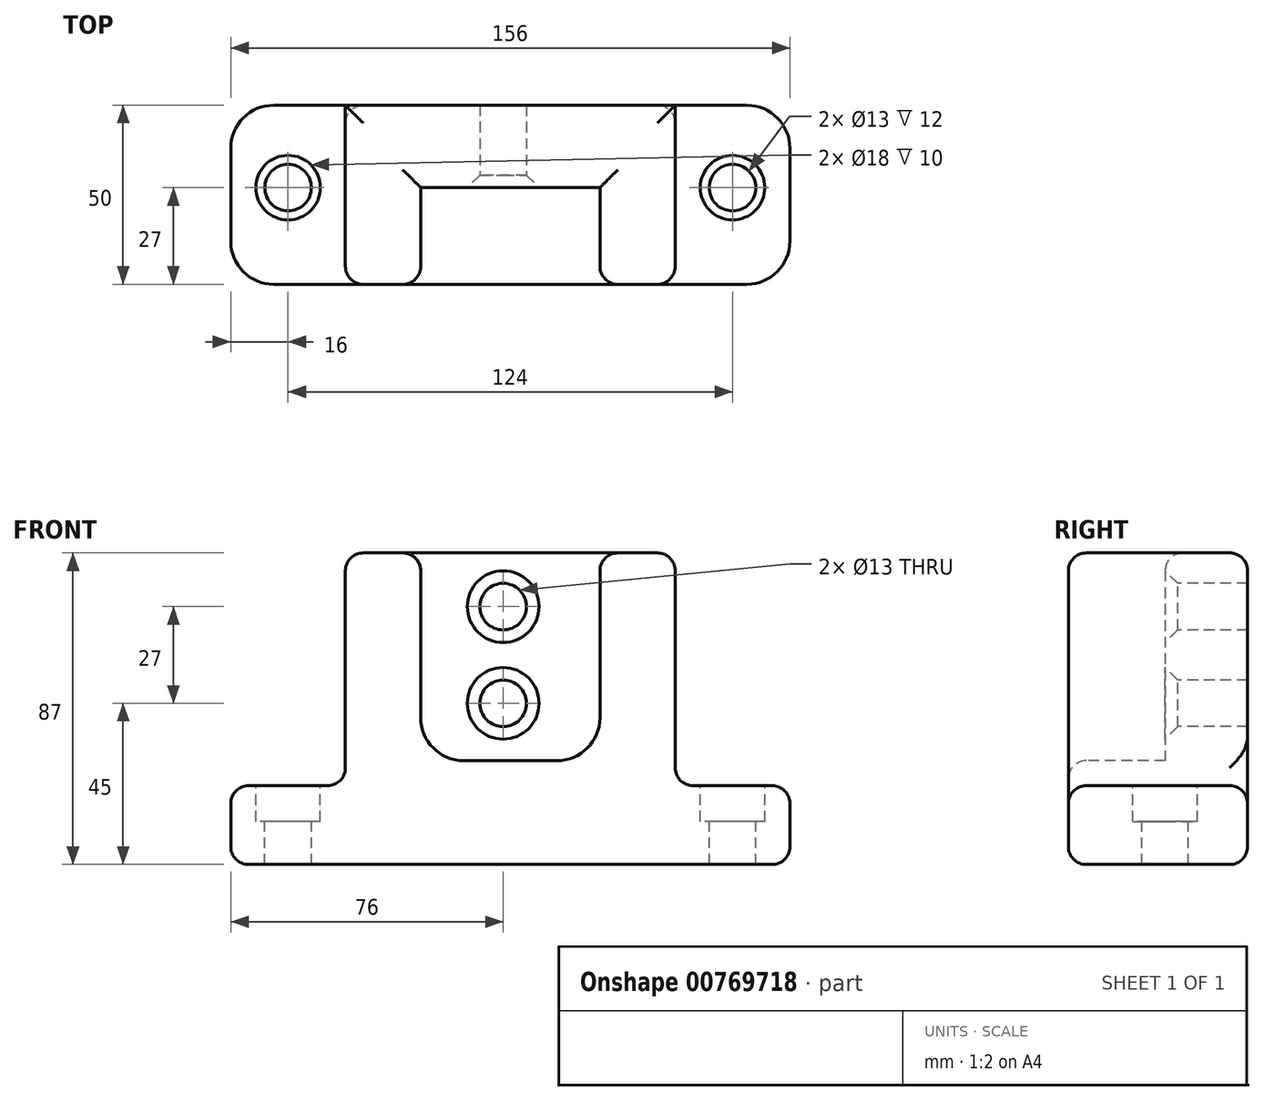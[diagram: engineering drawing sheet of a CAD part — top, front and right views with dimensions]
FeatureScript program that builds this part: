
annotation { "Feature Type Name" : "Feature", "Feature Type Description" : "" }
export const myFeature = defineFeature(function(context is Context, id is Id, definition is map)
    precondition{}
    {
        {
            var Q0;
            Q0=qCreatedBy(makeId("Top.planeOp"),FACE);
            var sketch = newSketch(context, id + "F0", { "sketchPlane" : qUnion([Q0])});
            skLineSegment(sketch, "E0.bottom", {"start": v(0, 0) * mm, "end": v(156, 0) * mm});
            skLineSegment(sketch, "E0.top", {"start": v(0, 50) * mm, "end": v(156, 50) * mm});
            skLineSegment(sketch, "E0.left", {"start": v(0, 0) * mm, "end": v(0, 50) * mm});
            skLineSegment(sketch, "E0.right", {"start": v(156, 0) * mm, "end": v(156, 50) * mm});
            skSolve(sketch);
        }
        {
            var Q0;
            Q0=makeQuery(id+"F0.imprint","IMPRINT",FACE,{"disambiguationData":[TD([[makeQuery(id+"F0.imprint","IMPRINT",EDGE,{"derivedFrom":sQuery(id+"F0.wireOp",EDGE,"E0.bottom")}),1.0]])]});
            extrude(context, id + "F1", {"entities" : qUnion([Q0]), "depth" : 87 * mm, "offsetDistance" : 25 * mm});
        }
        {
            var Q0;
            Q0=makeQuery(id+"F1.opExtrude","SWEPT_FACE",FACE,{"disambiguationData":[OSD([sQuery(id+"F0.wireOp",EDGE,"E0.bottom")])]});
            var sketch = newSketch(context, id + "F2", { "sketchPlane" : qUnion([Q0])});
            skLineSegment(sketch, "E1.bottom", {"start": v(0, 87) * mm, "end": v(32, 87) * mm});
            skLineSegment(sketch, "E1.top", {"start": v(0, 22) * mm, "end": v(32, 22) * mm});
            skLineSegment(sketch, "E1.left", {"start": v(0, 87) * mm, "end": v(0, 22) * mm});
            skLineSegment(sketch, "E1.right", {"start": v(32, 87) * mm, "end": v(32, 22) * mm});
            skLineSegment(sketch, "E2.bottom", {"start": v(156, 87) * mm, "end": v(124, 87) * mm});
            skLineSegment(sketch, "E2.top", {"start": v(156, 22) * mm, "end": v(124, 22) * mm});
            skLineSegment(sketch, "E2.left", {"start": v(156, 87) * mm, "end": v(156, 22) * mm});
            skLineSegment(sketch, "E2.right", {"start": v(124, 87) * mm, "end": v(124, 22) * mm});
            skSolve(sketch);
        }
        {
            var Q0;
            Q0 = qSketchRegion(id + "F2", true);
            extrude(context, id + "F3", {"entities" : qUnion([Q0]), "operationType" : NewBodyOperationType.REMOVE, "endBound" : BoundingType.UP_TO_NEXT, "oppositeDirection" : true, "depth" : 25 * mm, "offsetDistance" : 25 * mm});
        }
        {
            var Q0;
            Q0=makeQuery(id+"F1.opExtrude","SWEPT_FACE",FACE,{"disambiguationData":[OSD([sQuery(id+"F0.wireOp",EDGE,"E0.bottom")])]});
            var sketch = newSketch(context, id + "F4", { "sketchPlane" : qUnion([Q0])});
            skLineSegment(sketch, "E3.bottom", {"start": v(53, 87) * mm, "end": v(103, 87) * mm});
            skLineSegment(sketch, "E3.top", {"start": v(53, 29) * mm, "end": v(103, 29) * mm});
            skLineSegment(sketch, "E3.left", {"start": v(53, 87) * mm, "end": v(53, 29) * mm});
            skLineSegment(sketch, "E3.right", {"start": v(103, 87) * mm, "end": v(103, 29) * mm});
            skSolve(sketch);
        }
        {
            var Q0;
            Q0=makeQuery(id+"F4.imprint","IMPRINT",FACE,{"disambiguationData":[TD([[makeQuery(id+"F4.imprint","IMPRINT",EDGE,{"derivedFrom":sQuery(id+"F4.wireOp",EDGE,"E3.bottom")}),-1.0]])]});
            extrude(context, id + "F5", {"entities" : qUnion([Q0]), "operationType" : NewBodyOperationType.REMOVE, "oppositeDirection" : true, "depth" : 27 * mm, "offsetDistance" : 25 * mm});
        }
        {
            var Q0;
            Q0=makeQuery(id+"F3.boolean.opBoolean","COPY",FACE,{"derivedFrom":makeQuery(id+"F3.opExtrude","SWEPT_FACE",FACE,{"disambiguationData":[OSD([sQuery(id+"F2.wireOp",EDGE,"E2.top")])]})});
            var sketch = newSketch(context, id + "F6", { "sketchPlane" : qUnion([Q0])});
            skPoint(sketch, "E4", {"position": v(16, 27) * mm});
            skPoint(sketch, "E5", {"position": v(140, 27) * mm});
            skSolve(sketch);
        }
        {
            var Q0;
            Q0=sQuery(id+"F6.wireOp",VERTEX,"E4");
            var Q1;
            Q1=sQuery(id+"F6.wireOp",VERTEX,"E5");
            var Q2;
            Q2=makeQuery(id+"F1.opExtrude","SWEPT_BODY",BODY,{"disambiguationData":[OSD([sQuery(id+"F0.wireOp",EDGE,"E0.bottom"),sQuery(id+"F0.wireOp",EDGE,"E0.top"),sQuery(id+"F0.wireOp",EDGE,"E0.left"),sQuery(id+"F0.wireOp",EDGE,"E0.right")])]});
            hole(context, id + "F7", {"style" : HoleStyle.C_BORE, "endStyle" : HoleEndStyle.THROUGH, "holeDiameter" : 13 * mm, "cBoreDiameter" : 18 * mm, "cBoreDepth" : 10 * mm, "majorDiameter" : 5 * mm, "isTappedThrough" : true, "tappedDepth" : 12 * mm, "tapClearance" : 3, "locations" : qUnion([Q0, Q1]), "scope" : qUnion([Q2])});
        }
        {
            var Q0;
            Q0=makeQuery(id+"F5.boolean.opBoolean","COPY",FACE,{"derivedFrom":makeQuery(id+"F5.opExtrude","CAP_FACE",FACE,{"disambiguationData":[OSD([sQuery(id+"F4.wireOp",EDGE,"E3.bottom"),sQuery(id+"F4.wireOp",EDGE,"E3.top"),sQuery(id+"F4.wireOp",EDGE,"E3.left"),sQuery(id+"F4.wireOp",EDGE,"E3.right")])],"isStart":false})});
            var sketch = newSketch(context, id + "F8", { "sketchPlane" : qUnion([Q0])});
            skPoint(sketch, "E6", {"position": v(76, 72) * mm});
            skPoint(sketch, "E7", {"position": v(76, 45) * mm});
            skSolve(sketch);
        }
        {
            var Q0;
            Q0=sQuery(id+"F8.wireOp",VERTEX,"E6");
            var Q1;
            Q1=sQuery(id+"F8.wireOp",VERTEX,"E7");
            var Q2;
            Q2=makeQuery(id+"F1.opExtrude","SWEPT_BODY",BODY,{"disambiguationData":[OSD([sQuery(id+"F0.wireOp",EDGE,"E0.bottom"),sQuery(id+"F0.wireOp",EDGE,"E0.top"),sQuery(id+"F0.wireOp",EDGE,"E0.left"),sQuery(id+"F0.wireOp",EDGE,"E0.right")])]});
            hole(context, id + "F9", {"style" : HoleStyle.C_SINK, "endStyle" : HoleEndStyle.THROUGH, "holeDiameter" : 13 * mm, "cSinkDiameter" : 20 * mm, "cSinkAngle" : 90 * degree, "majorDiameter" : 5 * mm, "isTappedThrough" : true, "tappedDepth" : 12 * mm, "tapClearance" : 3, "locations" : qUnion([Q0, Q1]), "scope" : qUnion([Q2])});
        }
        {
            var Q0;
            Q0=makeQuery(id+"F1.opExtrude","SWEPT_EDGE",EDGE,{"disambiguationData":[OSD([sQuery(id+"F0.wireOp",EDGE,"E0.bottom"),sQuery(id+"F0.wireOp",EDGE,"E0.right")])]});
            var Q1;
            Q1=makeQuery(id+"F1.opExtrude","SWEPT_EDGE",EDGE,{"disambiguationData":[OSD([sQuery(id+"F0.wireOp",EDGE,"E0.top"),sQuery(id+"F0.wireOp",EDGE,"E0.right")])]});
            var Q2;
            Q2=makeQuery(id+"F5.boolean.opBoolean","COPY",EDGE,{"derivedFrom":makeQuery(id+"F5.opExtrude","SWEPT_EDGE",EDGE,{"disambiguationData":[OSD([sQuery(id+"F4.wireOp",EDGE,"E3.top"),sQuery(id+"F4.wireOp",EDGE,"E3.right")])]})});
            var Q3;
            Q3=makeQuery(id+"F5.boolean.opBoolean","COPY",EDGE,{"derivedFrom":makeQuery(id+"F5.opExtrude","SWEPT_EDGE",EDGE,{"disambiguationData":[OSD([sQuery(id+"F4.wireOp",EDGE,"E3.top"),sQuery(id+"F4.wireOp",EDGE,"E3.left")])]})});
            var Q4;
            Q4=makeQuery(id+"F1.opExtrude","SWEPT_EDGE",EDGE,{"disambiguationData":[OSD([sQuery(id+"F0.wireOp",EDGE,"E0.top"),sQuery(id+"F0.wireOp",EDGE,"E0.left")])]});
            var Q5;
            Q5=makeQuery(id+"F1.opExtrude","SWEPT_EDGE",EDGE,{"disambiguationData":[OSD([sQuery(id+"F0.wireOp",EDGE,"E0.bottom"),sQuery(id+"F0.wireOp",EDGE,"E0.left")])]});
            fillet(context, id + "F10", {"entities" : qUnion([Q0, Q1, Q2, Q3, Q4, Q5]), "radius" : 12 * mm, "tangentPropagation" : true, "allowEdgeOverflow" : false});
        }
        {
            var Q0;
            Q0=makeQuery(id+"F1.opExtrude","CAP_FACE",FACE,{"disambiguationData":[OSD([sQuery(id+"F0.wireOp",EDGE,"E0.bottom"),sQuery(id+"F0.wireOp",EDGE,"E0.top"),sQuery(id+"F0.wireOp",EDGE,"E0.left"),sQuery(id+"F0.wireOp",EDGE,"E0.right")])],"isStart":false});
            var Q1;
            Q1=makeQuery(id+"F1.opExtrude","SWEPT_FACE",FACE,{"disambiguationData":[OSD([sQuery(id+"F0.wireOp",EDGE,"E0.bottom")])]});
            var Q2;
            Q2=makeQuery(id+"F3.boolean.opBoolean","COPY",EDGE,{"derivedFrom":makeQuery(id+"F3.opExtrude","SWEPT_EDGE",EDGE,{"disambiguationData":[OSD([sQuery(id+"F2.wireOp",EDGE,"E2.top"),sQuery(id+"F2.wireOp",EDGE,"E2.right")])]})});
            var Q3;
            Q3=makeQuery(id+"F3.boolean.opBoolean","COPY",EDGE,{"derivedFrom":makeQuery(id+"F3.opExtrude","SWEPT_EDGE",EDGE,{"disambiguationData":[OSD([sQuery(id+"F2.wireOp",EDGE,"E1.top"),sQuery(id+"F2.wireOp",EDGE,"E1.right")])]})});
            fillet(context, id + "F11", {"entities" : qUnion([Q0, Q1, Q2, Q3]), "radius" : 5 * mm, "tangentPropagation" : true, "allowEdgeOverflow" : false});
        }
    });
